# Revit family: BasinTopStrainer-Vitra-UniversalSeries-A45148
name_source: partatom
category: Plumbing Fixtures
revit_build: Autodesk Revit 2017 (Build: 20160225_1515(x64)
units: mm (PartAtom-declared; Revit-internal decimal feet)

## family parameters
Always vertical = No
Cut with Voids When Loaded = No
OmniClass Number = 23.45.00.00
OmniClass Title = Sanitary, Laundry, and Cleaning Equipment
Part Type = Normal
Room Calculation Point = No
Round Connector Dimension = Use Diameter
Shared = No
Work Plane-Based = Yes

## types (5) — shared parameters
BIMobject category = Sanitary - Taps & Mixers
Brand = Vitra
CW Connection = No
Connection Diameter (mm) = 32 mm  [stored 0.104987 ft]
Default Elevation = 650 mm  [stored 2.13255 ft]
Depth(mm) = 68 mm
HW Connection = No
Height(mm) = 100 mm  [stored 0.328084 ft]
IFC Classification = Sanitary Terminal
Manufacturer = Vitra
Manufacturer country = Turkey
Manufacturer name = Vitra
Masterformat 2014 Code = 22 40 00
Masterformat 2014 Description = Plumbing Fixtures
MountingType = Pipe connection
NBS Reference Code = 62-24
NBS Reference Description = Drainage Traps
Number Of Connections = 1
OmniClass Code = 23-27 37 00
OmniClass Description = Liquid Traps
Product Type = Basic Grid Strainer
Product certification = https://vitraglobal.com
Product data url = https://www.vitraglobal.com
Product family = UniversalSeries
Product group = Basic Grid Strainer
Technical description = https://www.vitraglobal.com
UNSPSC Code = Traps and strainers
URL = https://vitraglobal.com
Uniclass 1.4 Code = L7254
Uniclass 1.4 Description = Traps for sinks and basins
Uniclass 2.0 Code = PR-62-24
Uniclass 2.0 Description = Drainage Traps
Uniclass 2015 Code = Pr_65_52_25
Uniclass 2015 Name = Drainage traps and accessories
Uniformat II Code = D2010
Uniformat II Description = Plumbing Fixtures
Warranty Period (Year) = 5
Waste Connection = Yes
Weight Net (Kg) = 0.338
Width(mm) = 68 mm
Youtube clip = https://www.youtube.com
zero-valued in all types: Cost, Nominal height, Nominal width

## per-type parameters (varying)
| type | Article No. (default) | Coating Material | Color | Installation instructions | Model | Product SKU |
| BasinGridStrainer-Vitra-UniversalSeries-A45148 | A45148 | Vitra-Chrome | Chrome |  | A45148 | A45148 |
| BasinGridStrainer-Vitra-UniversalSeries-A4514826 | A4514826 | Copper | Chrome |  | A4514826 | A4514826 |
| BasinGridStrainer-Vitra-UniversalSeries-A45148EXP | A45148EXP | Vitra-Chrome | Chrome |  | A45148EXP | A45148EXP |
| BasinGridStrainer-Vitra-UniversalSeries-A4514826EXP | A4514826EXP | Copper | Copper | https://cdn.vitra.com.tr | A4514826EXP | A4514826EXP |
| BasinGridStrainer-Vitra-UniversalSeries-A4514823EXP | A4514823EXP | Gold | Gold | https://cdn.vitra.com.tr | A4514823EXP | A4514823EXP |

note: [stored X ft] marks values corroborated as IEEE doubles in the binary element streams (Revit-internal decimal feet)

## geometry (parser evidence)
native form markers: Sweep x3
no freeform markers — native parametric forms only
